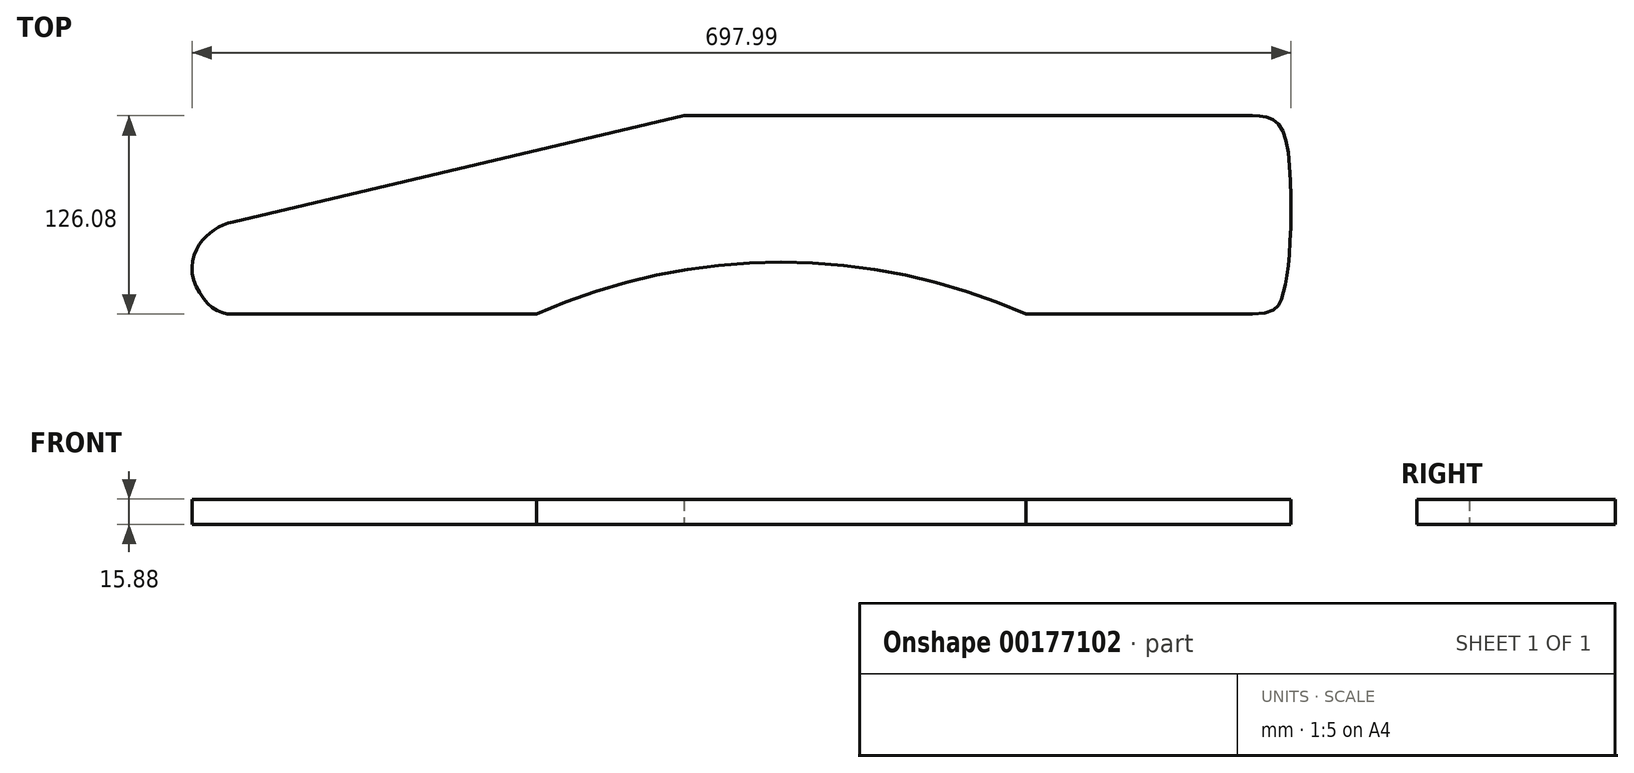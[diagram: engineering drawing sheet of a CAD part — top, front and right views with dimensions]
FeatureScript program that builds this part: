
annotation { "Feature Type Name" : "Feature", "Feature Type Description" : "" }
export const myFeature = defineFeature(function(context is Context, id is Id, definition is map)
    precondition{}
    {
        {
            var Q0;
            Q0=qCreatedBy(makeId("Top.planeOp"),FACE);
            var sketch = newSketch(context, id + "F0", { "sketchPlane" : qUnion([Q0])});
            skLineSegment(sketch, "E0", {"start": v(0, 0) * mm, "end": v(0, -127) * mm, "construction": true});
            skLineSegment(sketch, "E1", {"start": v(0, 0) * mm, "end": v(-700.09, 0) * mm, "construction": true});
            skLineSegment(sketch, "E2", {"start": v(-170.32, -126.08) * mm, "end": v(-26.52, -126.08) * mm});
            skLineSegment(sketch, "E3", {"start": v(-387.42, 0) * mm, "end": v(-26.53, 0) * mm});
            skFitSpline(sketch, "E4", {"points": [v(-26.53, 0) * mm, v(-15.6, -1.54) * mm, v(-7.4, -9.1) * mm, v(-2.16, -42.92) * mm, v(-3, -88.9) * mm, v(-5.94, -109.28) * mm, v(-9.72, -120.2) * mm, v(-26.52, -126.08) * mm], "startDerivative": vector(105.8, 0) * mm, "endDerivative": vector(-230.1, 0) * mm});
            skArc(sketch, "E5", {"start": v(-170.32, -126.08) * mm, "mid": v(-325.75, -92.94) * mm, "end": v(-481.17, -126.08) * mm});
            skLineSegment(sketch, "E6", {"start": v(-481.17, -126.08) * mm, "end": v(-673.87, -126.08) * mm});
            skFitSpline(sketch, "E7", {"points": [v(-673.87, -126.08) * mm, v(-688.17, -120.92) * mm, v(-699.53, -101.07) * mm, v(-695.97, -83.06) * mm, v(-686, -72.63) * mm, v(-673.87, -67.42) * mm], "startDerivative": vector(-87.83, 0) * mm, "endDerivative": vector(70.63, 16.63) * mm});
            skLineSegment(sketch, "E8", {"start": v(-673.87, -67.42) * mm, "end": v(-387.42, 0) * mm});
            skPoint(sketch, "E9", {"position": v(-350.04, 0) * mm});
            skSolve(sketch);
        }
        {
            var Q0;
            Q0 = qSketchRegion(id + "F0", true);
            extrude(context, id + "F1", {"entities" : qUnion([Q0]), "depth" : 15.88 * mm});
        }
    });
